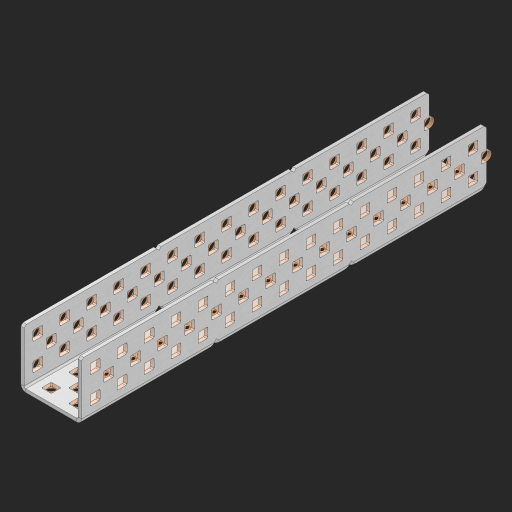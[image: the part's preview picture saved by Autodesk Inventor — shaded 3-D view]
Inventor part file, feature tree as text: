
AUTODESK INVENTOR PART (.ipt)
format: ipt  version: 2023 (Build 270158000, 158)  size: 1,843,712 bytes
history: native  units: in
note: dims shown in document units (in); Inventor stores cm internally (conversion verified against a paired STEP export)
features: other x186, extrude x178, sheet_metal_op x8, sketch x7, mirror x3, pattern_linear x2, chamfer x1
ambient origin geometry x8: Origin, YZ Plane, XZ Plane, XY Plane, X Axis, Y Axis, Z Axis, Center Point
bodies: Solid1 (feature_tree), Body (feature_tree)
feature tree (385):
  sheet_metal_op  "Flanges"
  sheet_metal_op  "Body Pattern"
  pattern_linear  "Center Pattern"  Spacing1=1.0in  [1 undecoded]
  other  "Arc Length"
  mirror  "Notch Mirror"
  pattern_linear  "Notch Pattern"  Spacing1=0.25in  [1 undecoded]
  other  "Diagonal Plane"
  mirror  "Flange 1"
  mirror  "Flange 2"
  chamfer  "End Chamfer"
  sketch  "Sketch1"  dims[d0=1.0in]
  other  "Plate1"
  sketch  "Sketch2"  dims[d1=7.5in]
  other  "Plate2"
  sheet_metal_op  "Bend1"
  sheet_metal_op  "Corner1"
  sketch  "Sketch8"  dims[d2=0.0625in]
  sketch  "Sketch9"  dims[d3=0.0625in]
  other  "Srf91"
  sheet_metal_op  "Body Pattern Sketch"
  other  "Srf92"
  sketch  "Sketch13"  dims[d4=0.0312in]
  sketch  "Sketch15"  dims[d5=0.125in]
  sketch  "Sketch16"  dims[d6=0.0625in d7=1.0in d8=90.0deg d9=0.0312in d10=0.25in d11=0.0625in d12=0.0625in d49=0.182in d50=0.02in d52=0.25in d53=0.0625in d54=0.0in d55=0.172in d56=1.0in d57=0.0in d60=5.9055in d62=0.5in d63=0.7874in d65=0.5in d85=0.1473in d86=0.1782in d88=0.04in d89=0.0625in d90=0.0in d91=0.04in d92=0.0491in d95=2.5in d96=0.04in d97=0.25in d98=45.0deg d99=0.25in d102=2.497in d106=0.182in d107=0.02in d108=0.5in d110=0.0625in d111=0.0in d112=0.172in d113=0.5in d114=0.0in d117=0.5in d118=0.5in d131=0.25in d132=0.25in]
  other  "Srf786"
  other  "Srf889"
  other  "Srf890"
  other  "Srf891"
  other  "Srf892"
  other  "Srf893"
  other  "Srf894"
  other  "Srf895"
  other  "Srf896"
  other  "Srf996"
  other  "Srf997"
  other  "Srf998"
  other  "Srf999"
  other  "Srf1000"
  other  "Srf1255"
  other  "Srf1315"
  other  "Srf1316"
  other  "Srf1317"
  other  "Srf1325"
  other  "Srf1326"
  other  "Srf1327"
  other  "Srf1328"
  other  "Srf1329"
  other  "Srf1330"
  other  "Srf1331"
  other  "Srf1332"
  other  "Srf1338"
  other  "Srf1339"
  other  "Srf1340"
  other  "Srf1341"
  other  "Srf1342"
  other  "Srf1369"
  other  "Srf1374"
  other  "Srf1375"
  other  "Srf1376"
  other  "Srf1384"
  other  "Srf1385"
  other  "Srf1386"
  other  "Srf1387"
  other  "Srf1388"
  other  "Srf1389"
  other  "Srf1390"
  other  "Srf1391"
  other  "Srf1397"
  other  "Srf1398"
  other  "Srf1399"
  other  "Srf1400"
  other  "Srf1401"
  other  "Srf1428"
  other  "Srf1433"
  other  "Srf1434"
  other  "Srf1473"
  other  "Srf1474"
  other  "Srf1475"
  other  "Srf1476"
  other  "Srf1477"
  other  "Srf1478"
  other  "Srf1479"
  other  "Srf1480"
  other  "Srf1481"
  other  "Srf1482"
  other  "Srf1483"
  other  "Srf1484"
  other  "Srf1485"
  other  "Srf1486"
  other  "Srf1487"
  other  "Srf1500"
  other  "Srf1501"
  other  "Srf1502"
  other  "Srf1503"
  other  "Srf1504"
  other  "Srf1505"
  other  "Srf1506"
  other  "Srf1507"
  other  "Srf1508"
  other  "Srf1509"
  other  "Srf1510"
  other  "Srf1511"
  other  "Srf1512"
  other  "Srf1513"
  other  "Srf1514"
  other  "Srf1515"
  other  "Srf1516"
  other  "Srf1517"
  other  "Srf1518"
  other  "Srf1519"
  other  "Srf1520"
  other  "Srf1521"
  other  "Srf1522"
  other  "Srf1523"
  other  "Srf1524"
  other  "Srf1525"
  other  "Srf1526"
  other  "Srf1527"
  other  "Srf1538"
  other  "Srf1539"
  other  "Srf1540"
  other  "Srf1541"
  other  "Srf1542"
  other  "Srf1543"
  other  "Srf1544"
  other  "Srf1545"
  other  "Srf1546"
  other  "Srf1547"
  other  "Srf1548"
  other  "Srf1549"
  other  "Srf1550"
  other  "Srf1551"
  other  "Srf1552"
  other  "Srf1553"
  other  "Srf1554"
  other  "Srf1555"
  other  "Srf1556"
  other  "Srf1557"
  other  "Srf1558"
  other  "Srf1559"
  other  "Srf1560"
  other  "Srf1561"
  other  "Srf1562"
  other  "Srf1563"
  other  "Srf1564"
  other  "Srf1565"
  other  "Srf1576"
  other  "Srf1577"
  other  "Srf1578"
  other  "Srf1579"
  other  "Srf1580"
  other  "Srf1581"
  other  "Srf1582"
  other  "Srf1583"
  other  "Srf1584"
  other  "Srf1585"
  other  "Srf1586"
  other  "Srf1587"
  other  "Srf1588"
  other  "Srf1589"
  other  "Srf1590"
  other  "Srf1591"
  other  "Srf1592"
  other  "Srf1593"
  other  "Srf1594"
  other  "Srf1595"
  other  "Srf1596"
  other  "Srf1597"
  other  "Srf1598"
  other  "Srf1599"
  other  "Srf1600"
  other  "Srf1601"
  other  "Srf1602"
  other  "Srf1603"
  other  "Srf1614"
  other  "Srf1615"
  other  "Srf1616"
  other  "Srf1617"
  other  "Srf1618"
  other  "Srf1619"
  other  "Srf1620"
  other  "Srf1621"
  other  "Srf1622"
  other  "Srf1623"
  other  "Srf1624"
  other  "Srf1625"
  other  "Srf1626"
  other  "Srf1627"
  other  "Srf1628"
  other  "Srf1629"
  other  "Srf1630"
  other  "Srf1631"
  other  "Srf1632"
  other  "Srf1633"
  other  "Srf1634"
  other  "Srf1635"
  other  "Srf1636"
  other  "Srf1637"
  other  "Srf1638"
  other  "Srf1639"
  other  "Srf1640"
  other  "Srf1641"
  sheet_metal_op  "Body Stamp"
  sheet_metal_op  "Body Circle"
  other  "Center Stamp"
  other  "Center Circle"
  sheet_metal_op  "Notch"
  extrude  "ExtrusionSrf92"  Depth=0.0625in
  extrude  "ExtrusionSrf889"  Depth=0.0625in
  extrude  "ExtrusionSrf890"  Depth=0.25in
  extrude  "ExtrusionSrf891"  Depth=0.02in
  extrude  "ExtrusionSrf892"  Depth=0.25in
  extrude  "ExtrusionSrf893"  Depth=0.0625in
  extrude  "ExtrusionSrf894"  TaperAngle=0.0deg  [1 undecoded]
  extrude  "ExtrusionSrf895"  Depth=0.25in
  extrude  "ExtrusionSrf896"  Depth=1.0in TaperAngle=0.0deg
  extrude  "ExtrusionSrf996"  Depth=0.25in
  extrude  "ExtrusionSrf997"  Depth=0.5in
  extrude  "ExtrusionSrf998"  Depth=0.25in
  extrude  "ExtrusionSrf999"  Depth=0.25in
  extrude  "ExtrusionSrf1000"  Depth=0.25in
  extrude  "ExtrusionSrf1255"  Depth=0.0625in
  extrude  "ExtrusionSrf1315"  TaperAngle=0.0deg  [1 undecoded]
  extrude  "ExtrusionSrf1316"  Depth=0.25in
  extrude  "ExtrusionSrf1355"  Depth=0.25in
  extrude  "ExtrusionSrf1356"  Depth=2.5in
  extrude  "ExtrusionSrf1357"  Depth=0.25in TaperAngle=45.0deg
  extrude  "ExtrusionSrf1358"  Depth=0.25in
  extrude  "ExtrusionSrf1359"  Depth=0.25in
  extrude  "ExtrusionSrf1360"  Depth=0.25in
  extrude  "ExtrusionSrf1361"  Depth=0.02in
  extrude  "ExtrusionSrf1362"  Depth=0.5in
  extrude  "ExtrusionSrf1363"  Depth=0.0625in
  extrude  "ExtrusionSrf1364"  TaperAngle=0.0deg  [1 undecoded]
  extrude  "ExtrusionSrf1365"  Depth=0.25in
  extrude  "ExtrusionSrf1366"  Depth=0.5in TaperAngle=0.0deg
  extrude  "ExtrusionSrf1367"  Depth=0.5in
  extrude  "ExtrusionSrf1368"  Depth=0.5in
  extrude  "ExtrusionSrf1369"  Depth=0.25in
  extrude  "ExtrusionSrf1374"  Depth=0.25in
  extrude  "ExtrusionSrf1375"  [1 undecoded]
  extrude  "ExtrusionSrf1414"  [1 undecoded]
  extrude  "ExtrusionSrf1415"  [1 undecoded]
  extrude  "ExtrusionSrf1416"  [1 undecoded]
  extrude  "ExtrusionSrf1417"  [1 undecoded]
  extrude  "ExtrusionSrf1418"  [1 undecoded]
  extrude  "ExtrusionSrf1419"  [1 undecoded]
  extrude  "ExtrusionSrf1420"  [1 undecoded]
  extrude  "ExtrusionSrf1421"  [1 undecoded]
  extrude  "ExtrusionSrf1422"  [1 undecoded]
  extrude  "ExtrusionSrf1423"  [1 undecoded]
  extrude  "ExtrusionSrf1424"  [1 undecoded]
  extrude  "ExtrusionSrf1425"  [1 undecoded]
  extrude  "ExtrusionSrf1426"  [1 undecoded]
  extrude  "ExtrusionSrf1427"  [1 undecoded]
  extrude  "ExtrusionSrf1428"  [1 undecoded]
  extrude  "ExtrusionSrf1433"  [1 undecoded]
  extrude  "ExtrusionSrf1434"  [1 undecoded]
  extrude  "ExtrusionSrf1473"  [1 undecoded]
  extrude  "ExtrusionSrf1474"  [1 undecoded]
  extrude  "ExtrusionSrf1475"  [1 undecoded]
  extrude  "ExtrusionSrf1476"  [1 undecoded]
  extrude  "ExtrusionSrf1477"  [1 undecoded]
  extrude  "ExtrusionSrf1478"  [1 undecoded]
  extrude  "ExtrusionSrf1479"  [1 undecoded]
  extrude  "ExtrusionSrf1480"  [1 undecoded]
  extrude  "ExtrusionSrf1481"  [1 undecoded]
  extrude  "ExtrusionSrf1482"  [1 undecoded]
  extrude  "ExtrusionSrf1483"  [1 undecoded]
  extrude  "ExtrusionSrf1484"  [1 undecoded]
  extrude  "ExtrusionSrf1485"  [1 undecoded]
  extrude  "ExtrusionSrf1486"  [1 undecoded]
  extrude  "ExtrusionSrf1487"  [1 undecoded]
  extrude  "ExtrusionSrf1500"  [1 undecoded]
  extrude  "ExtrusionSrf1501"  [1 undecoded]
  extrude  "ExtrusionSrf1502"  [1 undecoded]
  extrude  "ExtrusionSrf1503"  [1 undecoded]
  extrude  "ExtrusionSrf1504"  [1 undecoded]
  extrude  "ExtrusionSrf1505"  [1 undecoded]
  extrude  "ExtrusionSrf1506"  [1 undecoded]
  extrude  "ExtrusionSrf1507"  [1 undecoded]
  extrude  "ExtrusionSrf1508"  [1 undecoded]
  extrude  "ExtrusionSrf1509"  [1 undecoded]
  extrude  "ExtrusionSrf1510"  [1 undecoded]
  extrude  "ExtrusionSrf1511"  [1 undecoded]
  extrude  "ExtrusionSrf1512"  [1 undecoded]
  extrude  "ExtrusionSrf1513"  [1 undecoded]
  extrude  "ExtrusionSrf1514"  [1 undecoded]
  extrude  "ExtrusionSrf1515"  [1 undecoded]
  extrude  "ExtrusionSrf1516"  [1 undecoded]
  extrude  "ExtrusionSrf1517"  [1 undecoded]
  extrude  "ExtrusionSrf1518"  [1 undecoded]
  extrude  "ExtrusionSrf1519"  [1 undecoded]
  extrude  "ExtrusionSrf1520"  [1 undecoded]
  extrude  "ExtrusionSrf1521"  [1 undecoded]
  extrude  "ExtrusionSrf1522"  [1 undecoded]
  extrude  "ExtrusionSrf1523"  [1 undecoded]
  extrude  "ExtrusionSrf1524"  [1 undecoded]
  extrude  "ExtrusionSrf1525"  [1 undecoded]
  extrude  "ExtrusionSrf1526"  [1 undecoded]
  extrude  "ExtrusionSrf1527"  [1 undecoded]
  extrude  "ExtrusionSrf1538"  [1 undecoded]
  extrude  "ExtrusionSrf1539"  [1 undecoded]
  extrude  "ExtrusionSrf1540"  [1 undecoded]
  extrude  "ExtrusionSrf1541"  [1 undecoded]
  extrude  "ExtrusionSrf1542"  [1 undecoded]
  extrude  "ExtrusionSrf1543"  [1 undecoded]
  extrude  "ExtrusionSrf1544"  [1 undecoded]
  extrude  "ExtrusionSrf1545"  [1 undecoded]
  extrude  "ExtrusionSrf1546"  [1 undecoded]
  extrude  "ExtrusionSrf1547"  [1 undecoded]
  extrude  "ExtrusionSrf1548"  [1 undecoded]
  extrude  "ExtrusionSrf1549"  [1 undecoded]
  extrude  "ExtrusionSrf1550"  [1 undecoded]
  extrude  "ExtrusionSrf1551"  [1 undecoded]
  extrude  "ExtrusionSrf1552"  [1 undecoded]
  extrude  "ExtrusionSrf1553"  [1 undecoded]
  extrude  "ExtrusionSrf1554"  [1 undecoded]
  extrude  "ExtrusionSrf1555"  [1 undecoded]
  extrude  "ExtrusionSrf1556"  [1 undecoded]
  extrude  "ExtrusionSrf1557"  [1 undecoded]
  extrude  "ExtrusionSrf1558"  [1 undecoded]
  extrude  "ExtrusionSrf1559"  [1 undecoded]
  extrude  "ExtrusionSrf1560"  [1 undecoded]
  extrude  "ExtrusionSrf1561"  [1 undecoded]
  extrude  "ExtrusionSrf1562"  [1 undecoded]
  extrude  "ExtrusionSrf1563"  [1 undecoded]
  extrude  "ExtrusionSrf1564"  [1 undecoded]
  extrude  "ExtrusionSrf1565"  [1 undecoded]
  extrude  "ExtrusionSrf1576"  [1 undecoded]
  extrude  "ExtrusionSrf1577"  [1 undecoded]
  extrude  "ExtrusionSrf1578"  [1 undecoded]
  extrude  "ExtrusionSrf1579"  [1 undecoded]
  extrude  "ExtrusionSrf1580"  [1 undecoded]
  extrude  "ExtrusionSrf1581"  [1 undecoded]
  extrude  "ExtrusionSrf1582"  [1 undecoded]
  extrude  "ExtrusionSrf1583"  [1 undecoded]
  extrude  "ExtrusionSrf1584"  [1 undecoded]
  extrude  "ExtrusionSrf1585"  [1 undecoded]
  extrude  "ExtrusionSrf1586"  [1 undecoded]
  extrude  "ExtrusionSrf1587"  [1 undecoded]
  extrude  "ExtrusionSrf1588"  [1 undecoded]
  extrude  "ExtrusionSrf1589"  [1 undecoded]
  extrude  "ExtrusionSrf1590"  [1 undecoded]
  extrude  "ExtrusionSrf1591"  [1 undecoded]
  extrude  "ExtrusionSrf1592"  [1 undecoded]
  extrude  "ExtrusionSrf1593"  [1 undecoded]
  extrude  "ExtrusionSrf1594"  [1 undecoded]
  extrude  "ExtrusionSrf1595"  [1 undecoded]
  extrude  "ExtrusionSrf1596"  [1 undecoded]
  extrude  "ExtrusionSrf1597"  [1 undecoded]
  extrude  "ExtrusionSrf1598"  [1 undecoded]
  extrude  "ExtrusionSrf1599"  [1 undecoded]
  extrude  "ExtrusionSrf1600"  [1 undecoded]
  extrude  "ExtrusionSrf1601"  [1 undecoded]
  extrude  "ExtrusionSrf1602"  [1 undecoded]
  extrude  "ExtrusionSrf1603"  [1 undecoded]
  extrude  "ExtrusionSrf1614"  [1 undecoded]
  extrude  "ExtrusionSrf1615"  [1 undecoded]
  extrude  "ExtrusionSrf1616"  [1 undecoded]
  extrude  "ExtrusionSrf1617"  [1 undecoded]
  extrude  "ExtrusionSrf1618"  [1 undecoded]
  extrude  "ExtrusionSrf1619"  [1 undecoded]
  extrude  "ExtrusionSrf1620"  [1 undecoded]
  extrude  "ExtrusionSrf1621"  [1 undecoded]
  extrude  "ExtrusionSrf1622"  [1 undecoded]
  extrude  "ExtrusionSrf1623"  [1 undecoded]
  extrude  "ExtrusionSrf1624"  [1 undecoded]
  extrude  "ExtrusionSrf1625"  [1 undecoded]
  extrude  "ExtrusionSrf1626"  [1 undecoded]
  extrude  "ExtrusionSrf1627"  [1 undecoded]
  extrude  "ExtrusionSrf1628"  [1 undecoded]
  extrude  "ExtrusionSrf1629"  [1 undecoded]
  extrude  "ExtrusionSrf1630"  [1 undecoded]
  extrude  "ExtrusionSrf1631"  [1 undecoded]
  extrude  "ExtrusionSrf1632"  [1 undecoded]
  extrude  "ExtrusionSrf1633"  [1 undecoded]
  extrude  "ExtrusionSrf1634"  [1 undecoded]
  extrude  "ExtrusionSrf1635"  [1 undecoded]
  extrude  "ExtrusionSrf1636"  [1 undecoded]
  extrude  "ExtrusionSrf1637"  [1 undecoded]
  extrude  "ExtrusionSrf1638"  [1 undecoded]
  extrude  "ExtrusionSrf1639"  [1 undecoded]
  extrude  "ExtrusionSrf1640"  [1 undecoded]
  extrude  "ExtrusionSrf1641"  [1 undecoded]
note: 150 required parameter values undecoded (feature->parameter linkage not recoverable at this tier; creation-order binding heuristic only, values carry confidence <= 0.55)
